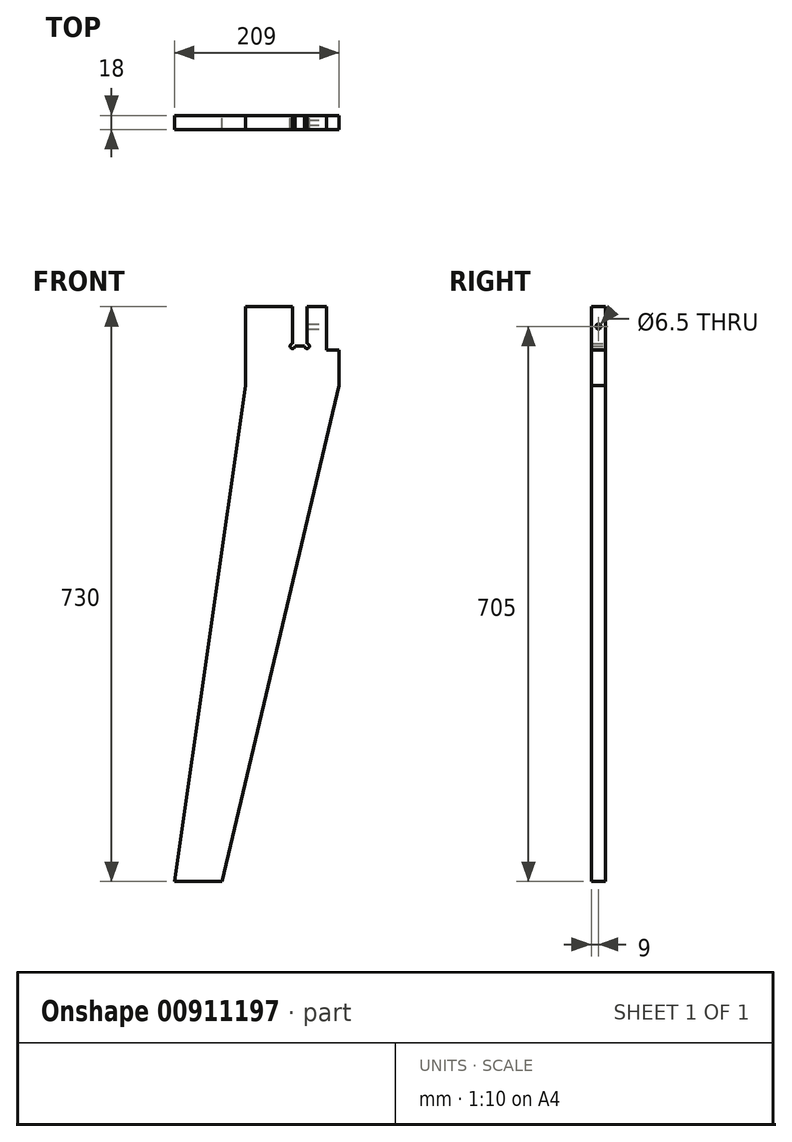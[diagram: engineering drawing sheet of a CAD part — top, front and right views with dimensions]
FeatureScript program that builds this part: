
annotation { "Feature Type Name" : "Feature", "Feature Type Description" : "" }
export const myFeature = defineFeature(function(context is Context, id is Id, definition is map)
    precondition{}
    {
        {
            var Q0;
            Q0=qCreatedBy(makeId("Front.planeOp"),FACE);
            var sketch = newSketch(context, id + "F0", { "sketchPlane" : qUnion([Q0])});
            skLineSegment(sketch, "E0", {"start": v(0, -100) * mm, "end": v(0, 0) * mm});
            skLineSegment(sketch, "E1", {"start": v(0, -100) * mm, "end": v(-90, -730) * mm});
            skLineSegment(sketch, "E2", {"start": v(-90, -730) * mm, "end": v(-30, -730) * mm});
            skLineSegment(sketch, "E3", {"start": v(59.75, -50) * mm, "end": v(78.25, -50) * mm});
            skLineSegment(sketch, "E4", {"start": v(0, 0) * mm, "end": v(59.75, 0) * mm});
            skLineSegment(sketch, "E5", {"start": v(59.75, 0) * mm, "end": v(59.75, -50) * mm});
            skLineSegment(sketch, "E6", {"start": v(78.25, 0) * mm, "end": v(78.25, -50) * mm});
            skLineSegment(sketch, "E7", {"start": v(59.75, -50) * mm, "end": v(59.75, -47) * mm});
            skLineSegment(sketch, "E8", {"start": v(59.75, -50) * mm, "end": v(62.75, -50) * mm});
            skLineSegment(sketch, "E9", {"start": v(78.25, -50) * mm, "end": v(75.25, -50) * mm});
            skLineSegment(sketch, "E10", {"start": v(78.25, -50) * mm, "end": v(78.25, -47) * mm});
            skArc(sketch, "E11", {"start": v(59.75, -47) * mm, "mid": v(57.63, -52.12) * mm, "end": v(62.75, -50) * mm});
            skArc(sketch, "E12", {"start": v(75.25, -50) * mm, "mid": v(80.37, -52.12) * mm, "end": v(78.25, -47) * mm});
            skLineSegment(sketch, "E13", {"start": v(119, -100) * mm, "end": v(-30, -730) * mm});
            skLineSegment(sketch, "E14", {"start": v(103, -55) * mm, "end": v(103, 0) * mm});
            skLineSegment(sketch, "E15", {"start": v(78.25, 0) * mm, "end": v(103, 0) * mm});
            skLineSegment(sketch, "E16", {"start": v(103, -25) * mm, "end": v(103, -55) * mm});
            skLineSegment(sketch, "E17", {"start": v(103, -55) * mm, "end": v(119, -55) * mm});
            skLineSegment(sketch, "E18", {"start": v(119, -55) * mm, "end": v(119, -100) * mm});
            skSolve(sketch);
        }
        {
            var Q0;
            Q0=makeQuery(id+"F0.imprint","IMPRINT",FACE,{"disambiguationData":[TD([[makeQuery(id+"F0.imprint","IMPRINT",EDGE,{"derivedFrom":sQuery(id+"F0.wireOp",EDGE,"QrxhmqMr-M4Cf-4XlO-vWOp-BbONrotqN2ly")}),-1.0]])]});
            var Q1;
            Q1=makeQuery(id+"F0.imprint","IMPRINT",FACE,{"disambiguationData":[TD([[makeQuery(id+"F0.imprint","IMPRINT",EDGE,{"derivedFrom":sQuery(id+"F0.wireOp",EDGE,"E0")}),-1.0]])]});
            extrude(context, id + "F1", {"entities" : qUnion([Q0, Q1]), "depth" : 18 * mm, "offsetDistance" : 25 * mm});
        }
        {
            var Q0;
            Q0=makeQuery(id+"F1.opExtrude","SWEPT_FACE",FACE,{"disambiguationData":[OSD([sQuery(id+"F0.wireOp",EDGE,"E14"),sQuery(id+"F0.wireOp",EDGE,"E16")])]});
            var sketch = newSketch(context, id + "F2", { "sketchPlane" : qUnion([Q0])});
            skLineSegment(sketch, "E19", {"start": v(-9, 0) * mm, "end": v(-9, -25) * mm});
            skCircle(sketch, "E20", {"center": v(-9, -25) * mm, "radius": 3.25 * mm});
            skSolve(sketch);
        }
        {
            var Q0;
            Q0=sQuery(id+"F2.wireOp",VERTEX,"E19.end");
            var Q1;
            Q1=makeQuery(id+"F1.opExtrude","SWEPT_BODY",BODY,{"disambiguationData":[OSD([sQuery(id+"F0.wireOp",EDGE,"E0"),sQuery(id+"F0.wireOp",EDGE,"E1"),sQuery(id+"F0.wireOp",EDGE,"E2"),sQuery(id+"F0.wireOp",EDGE,"E3"),sQuery(id+"F0.wireOp",EDGE,"E4"),sQuery(id+"F0.wireOp",EDGE,"E5"),sQuery(id+"F0.wireOp",EDGE,"E6"),sQuery(id+"F0.wireOp",EDGE,"E11"),sQuery(id+"F0.wireOp",EDGE,"E12"),sQuery(id+"F0.wireOp",EDGE,"E13"),sQuery(id+"F0.wireOp",EDGE,"E14"),sQuery(id+"F0.wireOp",EDGE,"E15"),sQuery(id+"F0.wireOp",EDGE,"E16"),sQuery(id+"F0.wireOp",EDGE,"E17"),sQuery(id+"F0.wireOp",EDGE,"E18")])]});
            hole(context, id + "F3", {"style" : HoleStyle.SIMPLE, "endStyle" : HoleEndStyle.BLIND, "holeDiameter" : 6.5 * mm, "majorDiameter" : 5 * mm, "holeDepth" : 25 * mm, "isTappedThrough" : true, "tappedDepth" : 12 * mm, "tapClearance" : 3, "locations" : qUnion([Q0]), "scope" : qUnion([Q1])});
        }
    });
